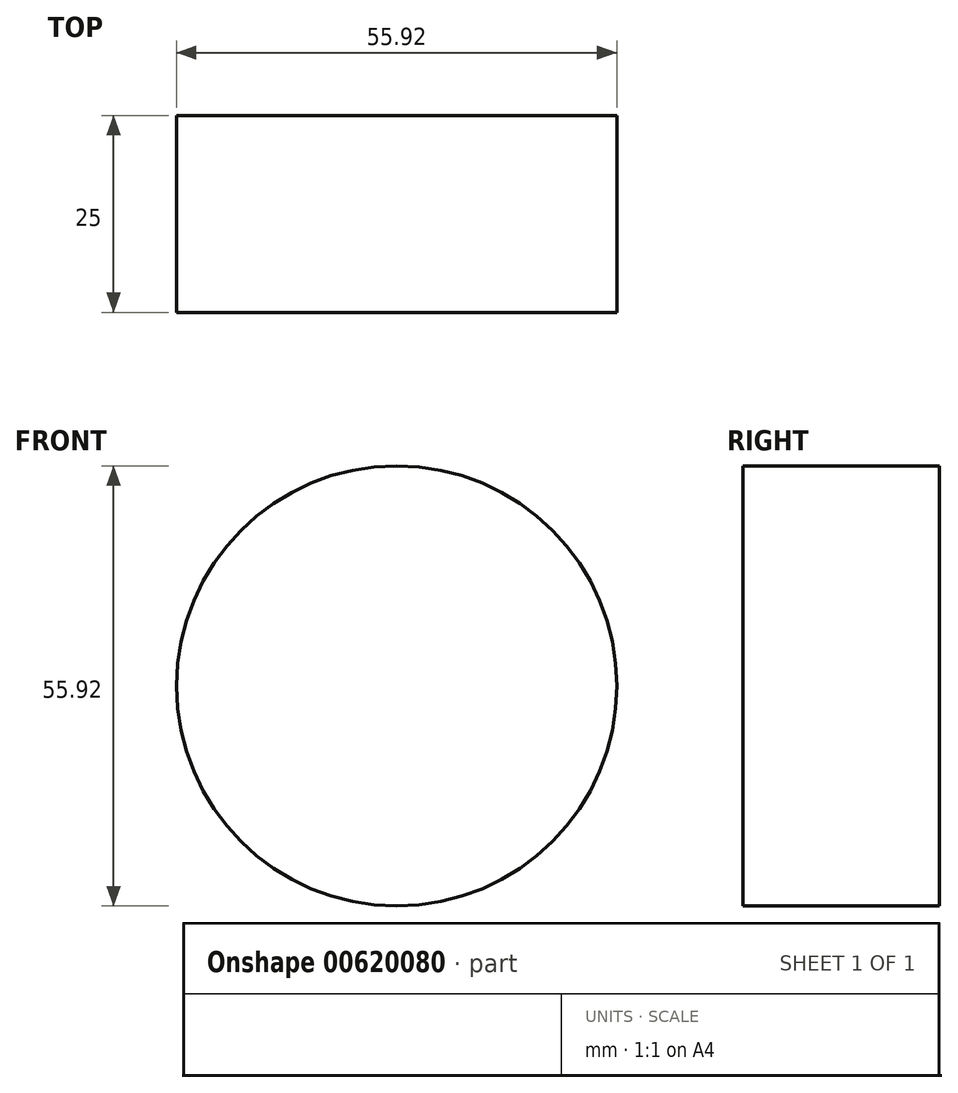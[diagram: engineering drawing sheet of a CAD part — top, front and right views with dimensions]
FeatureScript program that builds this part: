
annotation { "Feature Type Name" : "Feature", "Feature Type Description" : "" }
export const myFeature = defineFeature(function(context is Context, id is Id, definition is map)
    precondition{}
    {
        {
            var Q0;
            Q0=qCreatedBy(makeId("Front.planeOp"),FACE);
            var sketch = newSketch(context, id + "F0", { "sketchPlane" : qUnion([Q0])});
            skCircle(sketch, "E0", {"center": v(0, 0) * mm, "radius": 27.96 * mm});
            skSolve(sketch);
        }
        {
            var Q0;
            Q0=makeQuery(id+"F0.imprint","IMPRINT",FACE,{"disambiguationData":[TD([[makeQuery(id+"F0.imprint","IMPRINT",EDGE,{"derivedFrom":sQuery(id+"F0.wireOp",EDGE,"E0")}),1.0]])]});
            extrude(context, id + "F1", {"entities" : qUnion([Q0]), "depth" : 25 * mm, "offsetDistance" : 25 * mm});
        }
    });
